# Revit family: CREB2x2_2x4
name_source: partatom
category: Lighting Fixtures
units: mm (PartAtom-declared; Revit-internal decimal feet)

## family parameters
Always vertical = Yes
Cut with Voids When Loaded = No
Host = Ceiling
Light Source = Yes
OmniClass Number = 23.80.70.11.14.17
OmniClass Title = Direct/Indirect
Part Type = Normal
Room Calculation Point = No
Round Connector Dimension = Use Diameter
Shared = No

## types (6) — shared parameters
Assembly Code = D5020200
Color Filter = 16777215
Description = Cleanroom Recessed Ecology
Dimming Lamp Color Temperature Shift = <None>
Emit Shape Visible in Rendering = No
Emit from Rectangle Height = 0' - 0 1/32"
Emit from Rectangle Width = 1' - 11 3/4"
Housing Finish = Metal - Viscor - White
Lamp = LED
Lens Depth = 0' - 0 1/32"
Lens Finish = Acrylic - Viscor - Frosted White
Manufacturer = CERTOLUX by VISCOR
Model = CREB
Tilt Angle = 90.00°
URL = https://www.viscor.com
Voltage = 120 V
Water Shield = Polycarbonate - Viscor - Clear Lens
Width = 1' - 11 3/4"

## per-type parameters (varying)
| type | Apparent Load | Emit from Rectangle Length | Lamp Wattage | Length | Photometric Web File |
| CREB2X2-LED840K035LUNV | 31 VA | 1' - 11 3/4" | 31 VA | 1' - 11 3/4" | CREB2x2-LED840K035LUNV-P73P45.ies |
| CREB2X2-LED840K050LUNV | 38 VA | 1' - 11 3/4" | 38 VA | 1' - 11 3/4" | CREB2x2-LED840K050LUNV-P73P45.ies |
| CREB2X4-LED840K035LUNV | 31 VA | 3' - 11 3/4" | 31 VA | 3' - 11 3/4" | CREB2x4-LED840K035LUNV-P73P45.ies |
| CREB2X4-LED840K050LUNV | 38 VA | 3' - 11 3/4" | 38 VA | 3' - 11 3/4" | CREB2x4-LED840K050LUNV-P73P45.ies |
| CREB2X4-LED840K070LUNV | 57 VA | 3' - 11 3/4" | 57 VA | 3' - 11 3/4" | CREB2x4-LED840K070LUNV-P73P45.ies |
| CREB2X4-LED840K090LUNV | 81 VA | 3' - 11 3/4" | 81 VA | 3' - 11 3/4" | CREB2x4-LED840K090LUNV-P73P45.ies |

## geometry (parser evidence)
native form markers: Sweep x3
no freeform markers — native parametric forms only
